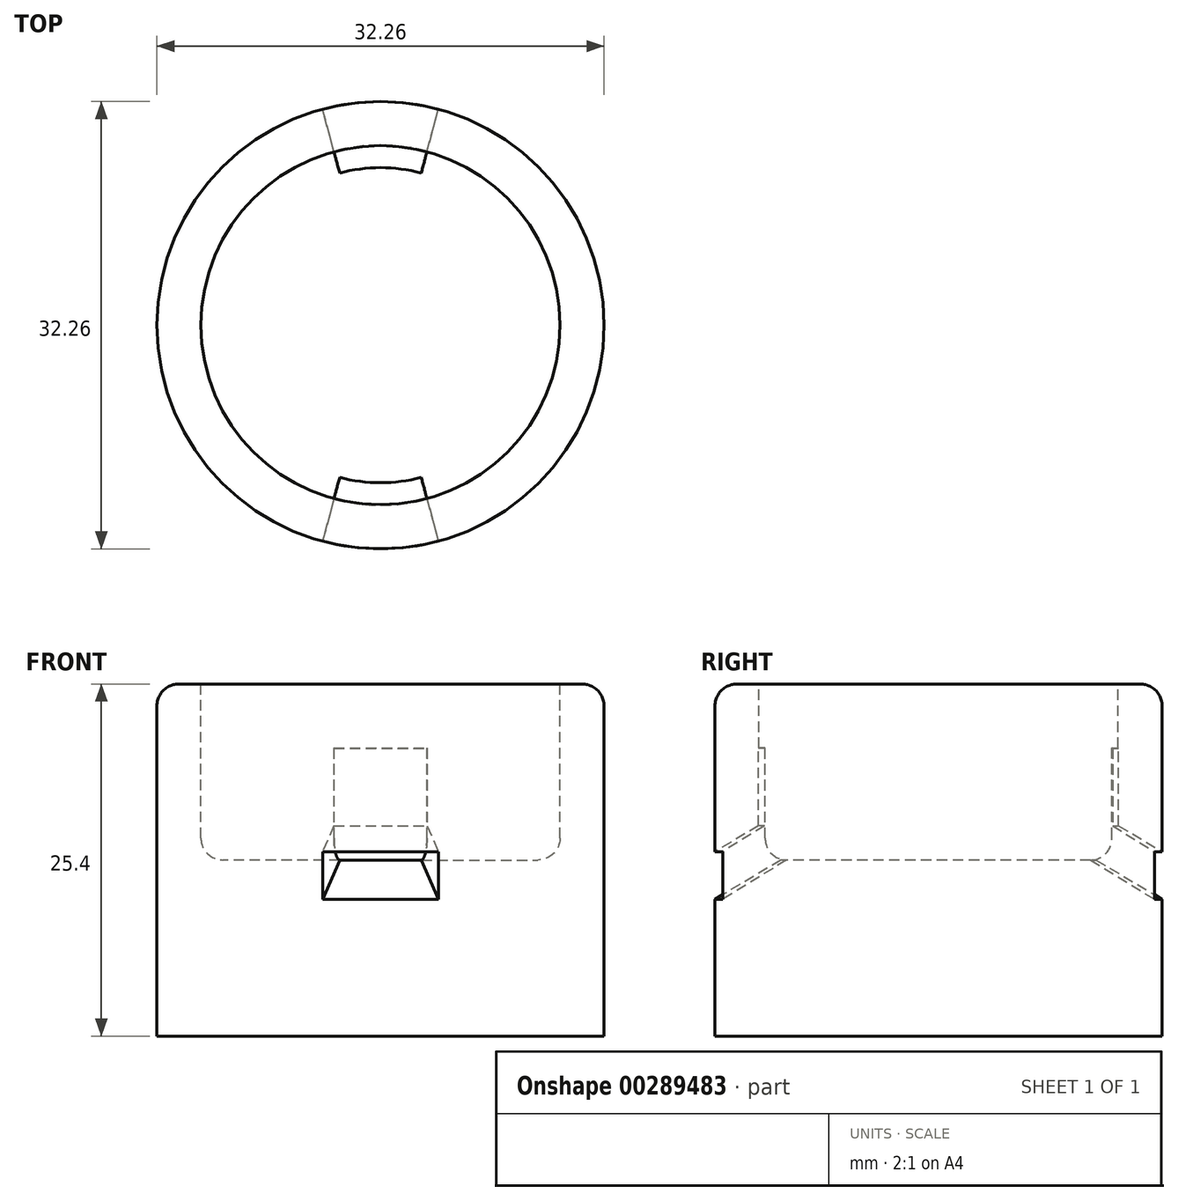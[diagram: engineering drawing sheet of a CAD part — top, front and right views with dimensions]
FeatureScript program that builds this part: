
annotation { "Feature Type Name" : "Feature", "Feature Type Description" : "" }
export const myFeature = defineFeature(function(context is Context, id is Id, definition is map)
    precondition{}
    {
        {
            var Q0;
            Q0=qCreatedBy(makeId("Top.planeOp"),FACE);
            var sketch = newSketch(context, id + "F0", { "sketchPlane" : qUnion([Q0])});
            skCircle(sketch, "E0", {"center": v(0, 0) * mm, "radius": 12.95 * mm});
            skCircle(sketch, "E1", {"center": v(0, 0) * mm, "radius": 12.7 * mm});
            skSolve(sketch);
        }
        {
            var Q0;
            Q0=qCreatedBy(makeId("Top.planeOp"),FACE);
            var sketch = newSketch(context, id + "F1", { "sketchPlane" : qUnion([Q0])});
            skCircle(sketch, "E2.0", {"center": v(0, 0) * mm, "radius": 12.95 * mm, "construction": true});
            skCircle(sketch, "E3", {"center": v(0, 0) * mm, "radius": 16.13 * mm});
            skSolve(sketch);
        }
        {
            var Q0;
            Q0 = qSketchRegion(id + "F1", true);
            extrude(context, id + "F2", {"entities" : qUnion([Q0]), "depth" : 25.4 * mm});
        }
        {
            var Q0;
            Q0=makeQuery(id+"F2.opExtrude","CAP_FACE",FACE,{"disambiguationData":[OSD([sQuery(id+"F1.wireOp",EDGE,"E3")])],"isStart":false});
            var sketch = newSketch(context, id + "F3", { "sketchPlane" : qUnion([Q0])});
            skCircle(sketch, "E4.0", {"center": v(0, 0) * mm, "radius": 12.95 * mm});
            skSolve(sketch);
        }
        {
            var Q0;
            Q0 = qSketchRegion(id + "F3", true);
            extrude(context, id + "F4", {"entities" : qUnion([Q0]), "operationType" : NewBodyOperationType.REMOVE, "oppositeDirection" : true, "depth" : 12.7 * mm});
        }
        {
            var Q0;
            Q0=makeQuery(id+"F2.opExtrude","CAP_EDGE",EDGE,{"disambiguationData":[OSD([sQuery(id+"F1.wireOp",EDGE,"E3")])],"isStart":false});
            var Q1;
            Q1=makeQuery(id+"F4.boolean.opBoolean","COPY",EDGE,{"derivedFrom":makeQuery(id+"F4.opExtrude","CAP_EDGE",EDGE,{"disambiguationData":[OSD([sQuery(id+"F3.wireOp",EDGE,"E4.0")])],"isStart":true})});
            var Q2;
            Q2=makeQuery(id+"F4.boolean.opBoolean","COPY",EDGE,{"derivedFrom":makeQuery(id+"F4.opExtrude","CAP_EDGE",EDGE,{"disambiguationData":[OSD([sQuery(id+"F3.wireOp",EDGE,"E4.0")])],"isStart":false})});
            fillet(context, id + "F5", {"entities" : qUnion([Q0, Q1, Q2]), "radius" : 1.59 * mm, "tangentPropagation" : true, "allowEdgeOverflow" : false});
        }
        {
            var Q0;
            Q0=qCreatedBy(makeId("Right.planeOp"),FACE);
            var sketch = newSketch(context, id + "F6", { "sketchPlane" : qUnion([Q0])});
            skLineSegment(sketch, "E5.0.0", {"start": v(-11.37, 12.7) * mm, "end": v(11.37, 12.7) * mm, "construction": true});
            skArc(sketch, "E6", {"start": v(-11.56, 15.86) * mm, "mid": v(-11.27, 12.7) * mm, "end": v(-11.37, 15.88) * mm, "construction": true});
            skArc(sketch, "E7", {"start": v(10.6, 12.9) * mm, "mid": v(12.73, 13.48) * mm, "end": v(12.23, 15.62) * mm});
            skLineSegment(sketch, "E8", {"start": v(12.95, 36.51) * mm, "end": v(12.95, 16.48) * mm, "construction": true});
            skLineSegment(sketch, "E9", {"start": v(-12.95, 26.99) * mm, "end": v(-12.95, 36.51) * mm, "construction": true});
            skLineSegment(sketch, "E10", {"start": v(-14.54, 25.4) * mm, "end": v(14.54, 25.4) * mm, "construction": true});
            skArc(sketch, "E11", {"start": v(-14.34, 25.39) * mm, "mid": v(-14.44, 25.4) * mm, "end": v(-14.54, 25.4) * mm, "construction": true});
            skArc(sketch, "E12", {"start": v(14.54, 25.4) * mm, "mid": v(14.44, 25.4) * mm, "end": v(14.34, 25.39) * mm, "construction": true});
            skLineSegment(sketch, "E13", {"start": v(16.13, 36.51) * mm, "end": v(16.13, 0) * mm, "construction": true});
            skLineSegment(sketch, "E14", {"start": v(10, 15.1) * mm, "end": v(11.37, 14.29) * mm, "construction": true});
            skLineSegment(sketch, "E15", {"start": v(10, 15.1) * mm, "end": v(16.13, 11.46) * mm, "construction": true});
            skLineSegment(sketch, "E16", {"start": v(11.37, 12.7) * mm, "end": v(16.13, 9.87) * mm});
            skLineSegment(sketch, "E17", {"start": v(12.23, 15.62) * mm, "end": v(16.13, 13.3) * mm});
            skLineSegment(sketch, "E18", {"start": v(16.13, 13.3) * mm, "end": v(16.13, 9.87) * mm});
            skLineSegment(sketch, "E19", {"start": v(0, 0) * mm, "end": v(0, 14.06) * mm, "construction": true});
            skLineSegment(sketch, "E20.MirrorCS", {"start": v(-11.37, 12.7) * mm, "end": v(-16.13, 9.87) * mm});
            skLineSegment(sketch, "E21.MirrorCS", {"start": v(-12.23, 15.62) * mm, "end": v(-16.13, 13.3) * mm});
            skArc(sketch, "E22.MirrorCS", {"start": v(-10.6, 12.9) * mm, "mid": v(-12.73, 13.48) * mm, "end": v(-12.23, 15.62) * mm});
            skLineSegment(sketch, "E23", {"start": v(-16.13, 13.3) * mm, "end": v(-16.13, 9.87) * mm});
            skLineSegment(sketch, "E24", {"start": v(12.23, 15.62) * mm, "end": v(12.23, 21.52) * mm});
            skLineSegment(sketch, "E25", {"start": v(12.23, 21.52) * mm, "end": v(13, 21.52) * mm});
            skLineSegment(sketch, "E26", {"start": v(13, 21.52) * mm, "end": v(13, 15.17) * mm});
            skLineSegment(sketch, "E27.MirrorCS", {"start": v(-12.23, 15.62) * mm, "end": v(-12.23, 21.52) * mm});
            skLineSegment(sketch, "E28.MirrorCS", {"start": v(-13, 21.52) * mm, "end": v(-13, 15.17) * mm});
            skLineSegment(sketch, "E29.MirrorCS", {"start": v(-12.23, 21.52) * mm, "end": v(-13, 21.52) * mm});
            skSolve(sketch);
        }
        {
            var Q0;
            Q0=makeQuery(id+"F6.imprint","IMPRINT",FACE,{"disambiguationData":[TD([[makeQuery(id+"F6.imprint","IMPRINT",EDGE,{"derivedFrom":sQuery(id+"F6.wireOp",EDGE,"E7")}),-1.0]])]});
            var Q1;
            Q1=makeQuery(id+"F6.imprint","IMPRINT",FACE,{"disambiguationData":[TD([[makeQuery(id+"F6.imprint","IMPRINT",EDGE,{"derivedFrom":sQuery(id+"F6.wireOp",EDGE,"E20.MirrorCS")}),-1.0]])]});
            var Q2;
            {var subQ0=sQuery(id+"F6.wireOp",EDGE,"E24");Q2=makeQuery(id+"F6.imprint","IMPRINT",FACE,{"disambiguationData":[TD([[makeQuery(id+"F6.imprint","IMPRINT",EDGE,{"derivedFrom":subQ0}),-1.0]])]});}
            var Q3;
            {var subQ0=sQuery(id+"F6.wireOp",EDGE,"E27.MirrorCS");Q3=makeQuery(id+"F6.imprint","IMPRINT",FACE,{"disambiguationData":[TD([[makeQuery(id+"F6.imprint","IMPRINT",EDGE,{"derivedFrom":subQ0}),1.0]])]});}
            var Q4;
            Q4=sQuery(id+"F6.wireOp",EDGE,"E19");
            revolve(context, id + "F7", {"operationType" : NewBodyOperationType.REMOVE, "entities" : qUnion([Q0, Q1, Q2, Q3]), "axis" : qUnion([Q4]), "revolveType" : RevolveType.SYMMETRIC, "oppositeDirection" : true, "angle" : 30 * degree});
        }
        {
            var Q0;
            Q0=makeQuery(id+"F7.boolean.opBoolean","COPY",EDGE,{"derivedFrom":makeQuery(id+"F7.opRevolve","SWEPT_EDGE",EDGE,{"disambiguationData":[OSD([sQuery(id+"F6.wireOp",EDGE,"E28.MirrorCS"),sQuery(id+"F6.wireOp",EDGE,"E29.MirrorCS")])]})});
            var Q1;
            Q1=makeQuery(id+"F7.boolean.opBoolean","COPY",EDGE,{"derivedFrom":makeQuery(id+"F7.opRevolve","SWEPT_EDGE",EDGE,{"disambiguationData":[OSD([sQuery(id+"F6.wireOp",EDGE,"E25"),sQuery(id+"F6.wireOp",EDGE,"E26")])]})});
            chamfer(context, id + "F8", {"entities" : qUnion([Q0, Q1]), "width" : 0.76 * mm, "tangentPropagation" : true});
        }
    });
